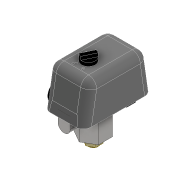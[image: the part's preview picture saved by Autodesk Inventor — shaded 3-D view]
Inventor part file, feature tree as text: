
AUTODESK INVENTOR PART (.ipt)
format: ipt  version: 2022 (Build 260153000, 153)  size: 388,096 bytes
history: native  units: mm
features: sketch x17, extrude x16, thread x2, other x2, fillet x2
ambient origin geometry x8: Origin, YZ Plane, XZ Plane, XY Plane, X Axis, Y Axis, Z Axis, Center Point
bodies: Solid1 (feature_tree), Solid2 (feature_tree), Solid3 (feature_tree), Solid4 (feature_tree), Solid5 (feature_tree), Solid6 (feature_tree), Solid7 (feature_tree), Solid8 (feature_tree), Solid9 (feature_tree)
feature tree (39):
  extrude  "Extrusion1"  Depth=3.0mm TaperAngle=0.0deg
  extrude  "Extrusion2"  Depth=3.0mm TaperAngle=0.0deg
  thread  "Thread1"  [1 undecoded]
  extrude  "Extrusion3"  Depth=10.0mm TaperAngle=0.0deg
  extrude  "Extrusion4"  Depth=2.0mm TaperAngle=0.0deg
  extrude  "Extrusion5"  Depth=14.0mm
  thread  "Thread2"  [1 undecoded]
  extrude  "Extrusion6"  Depth=3.0mm
  extrude  "Extrusion7"  Depth=20.0mm
  extrude  "Extrusion8"  Depth=1.0mm TaperAngle=0.0deg
  other  "Decal1"
  extrude  "Extrusion9"  Depth=12.0mm TaperAngle=0.0deg
  extrude  "Extrusion10"  Depth=12.0mm
  fillet  "Fillet1"  Radius=36.072mm
  fillet  "Fillet2"  Radius=5.0mm
  extrude  "Extrusion11"  Depth=1.0mm TaperAngle=0.0deg
  extrude  "Extrusion12"  Depth=4.0mm TaperAngle=0.0deg
  extrude  "Extrusion13"  [1 undecoded]
  extrude  "Extrusion14"  [1 undecoded]
  extrude  "Extrusion15"  [1 undecoded]
  extrude  "Extrusion16"  [1 undecoded]
  sketch  "Sketch1"  dims[d0=14.0mm d1=3.0mm d2=0.0mm]
  sketch  "Sketch2"  dims[d3=10.0mm d4=0.0mm d5=3.0mm d6=0.0mm d7=40.0mm d8=0.0mm]
  sketch  "Sketch3"  dims[d9=16.0mm d10=10.0mm d11=0.0mm]
  sketch  "Sketch4"  dims[d12=10.949mm d13=2.0mm d14=0.0mm]
  sketch  "Sketch5"  dims[d15=2.0mm d16=0.0mm d17=14.0mm d18=14.0mm]
  sketch  "Sketch6"  dims[d19=3.0mm d20=0.0mm d21=29.041mm]
  sketch  "Sketch7"  dims[d22=20.0mm d23=0.0mm d24=26.679mm]
  sketch  "Sketch8"  dims[d25=10.0mm d26=0.0mm d28=1.0mm d29=0.0mm]
  sketch  "Sketch9"  dims[d30=12.0mm d31=60.0mm d32=0.0mm]
  other  "Image1"
  sketch  "Sketch10"  dims[d33=12.0mm d34=12.0mm d35=36.072mm d36=0.0mm d37=5.0mm d38=0.0mm]
  sketch  "Sketch11"  dims[d41=5.0mm d42=0.0mm d43=1.0mm d44=0.0mm]
  sketch  "Sketch13"  dims[d45=15.0mm d46=0.0mm d47=4.0mm d48=0.0mm]
  sketch  "Sketch14"
  sketch  "Sketch15"
  sketch  "Sketch16"
  sketch  "Sketch17"
  sketch  "Sketch18"
note: 6 required parameter values undecoded (feature->parameter linkage not recoverable at this tier; creation-order binding heuristic only, values carry confidence <= 0.55)
